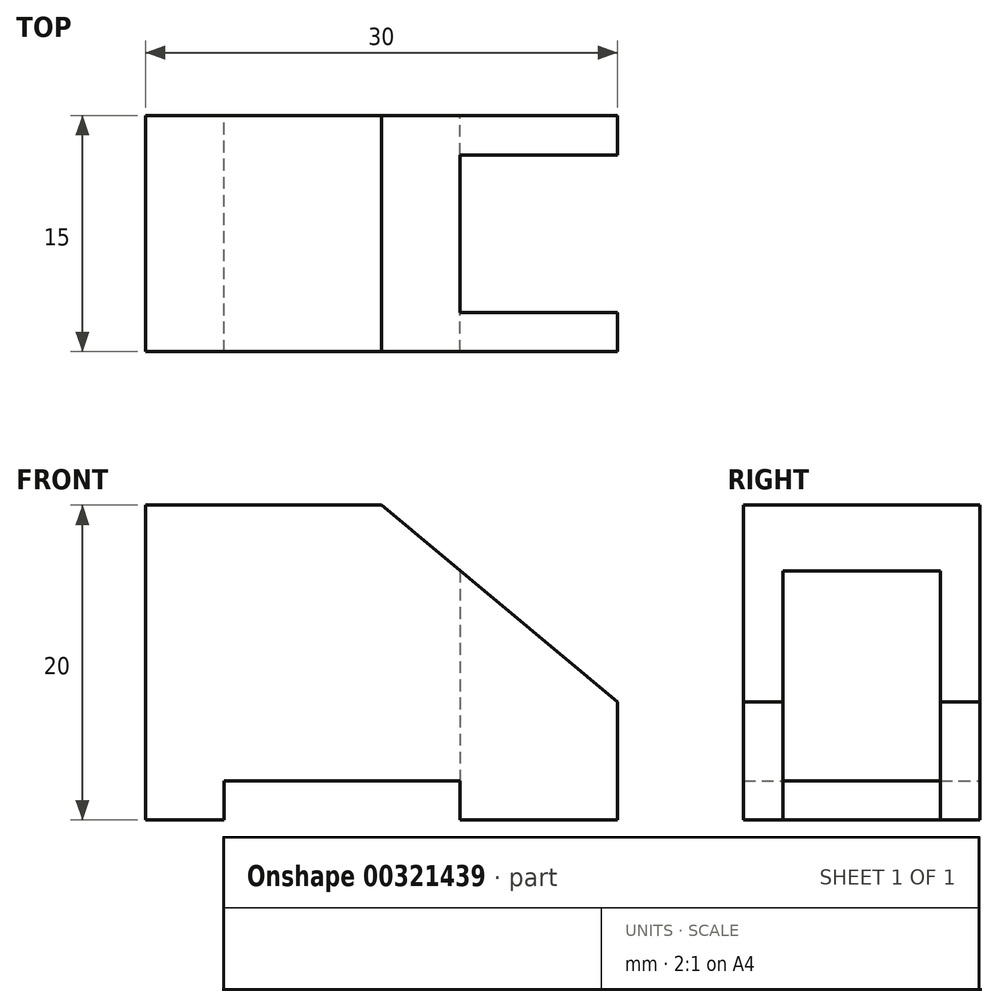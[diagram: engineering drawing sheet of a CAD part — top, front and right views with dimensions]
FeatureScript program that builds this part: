
annotation { "Feature Type Name" : "Feature", "Feature Type Description" : "" }
export const myFeature = defineFeature(function(context is Context, id is Id, definition is map)
    precondition{}
    {
        {
            var Q0;
            Q0=qCreatedBy(makeId("Front.planeOp"),FACE);
            var sketch = newSketch(context, id + "F0", { "sketchPlane" : qUnion([Q0])});
            skLineSegment(sketch, "E0.bottom", {"start": v(0, 0) * mm, "end": v(30, 0) * mm});
            skLineSegment(sketch, "E0.top", {"start": v(0, 20) * mm, "end": v(30, 20) * mm});
            skLineSegment(sketch, "E0.left", {"start": v(0, 0) * mm, "end": v(0, 20) * mm});
            skLineSegment(sketch, "E0.right", {"start": v(30, 0) * mm, "end": v(30, 20) * mm});
            skSolve(sketch);
        }
        {
            var Q0;
            Q0 = qSketchRegion(id + "F0", true);
            extrude(context, id + "F1", {"entities" : qUnion([Q0]), "depth" : 15 * mm});
        }
        {
            var Q0;
            Q0=qCreatedBy(makeId("Front.planeOp"),FACE);
            var sketch = newSketch(context, id + "F2", { "sketchPlane" : qUnion([Q0])});
            skLineSegment(sketch, "E1.bottom", {"start": v(5, 0) * mm, "end": v(20, 0) * mm});
            skLineSegment(sketch, "E1.top", {"start": v(5, 2.5) * mm, "end": v(20, 2.5) * mm});
            skLineSegment(sketch, "E1.left", {"start": v(5, 0) * mm, "end": v(5, 2.5) * mm});
            skLineSegment(sketch, "E1.right", {"start": v(20, 0) * mm, "end": v(20, 2.5) * mm});
            skLineSegment(sketch, "E2", {"start": v(15, 20) * mm, "end": v(30, 7.5) * mm});
            skLineSegment(sketch, "E3", {"start": v(30, 7.5) * mm, "end": v(30, 20) * mm});
            skLineSegment(sketch, "E4", {"start": v(30, 20) * mm, "end": v(15, 20) * mm});
            skSolve(sketch);
        }
        {
            var Q0;
            Q0 = qSketchRegion(id + "F2", true);
            extrude(context, id + "F3", {"entities" : qUnion([Q0]), "operationType" : NewBodyOperationType.REMOVE, "endBound" : BoundingType.THROUGH_ALL, "depth" : 25 * mm});
        }
        {
            var Q0;
            Q0=qCreatedBy(makeId("Top.planeOp"),FACE);
            var sketch = newSketch(context, id + "F4", { "sketchPlane" : qUnion([Q0])});
            skLineSegment(sketch, "E5.bottom", {"start": v(20, -2.5) * mm, "end": v(30, -2.5) * mm});
            skLineSegment(sketch, "E5.top", {"start": v(20, -12.5) * mm, "end": v(30, -12.5) * mm});
            skLineSegment(sketch, "E5.left", {"start": v(20, -2.5) * mm, "end": v(20, -12.5) * mm});
            skLineSegment(sketch, "E5.right", {"start": v(30, -2.5) * mm, "end": v(30, -12.5) * mm});
            skSolve(sketch);
        }
        {
            var Q0;
            Q0 = qSketchRegion(id + "F4", true);
            extrude(context, id + "F5", {"entities" : qUnion([Q0]), "operationType" : NewBodyOperationType.REMOVE, "endBound" : BoundingType.THROUGH_ALL, "depth" : 25 * mm});
        }
    });
